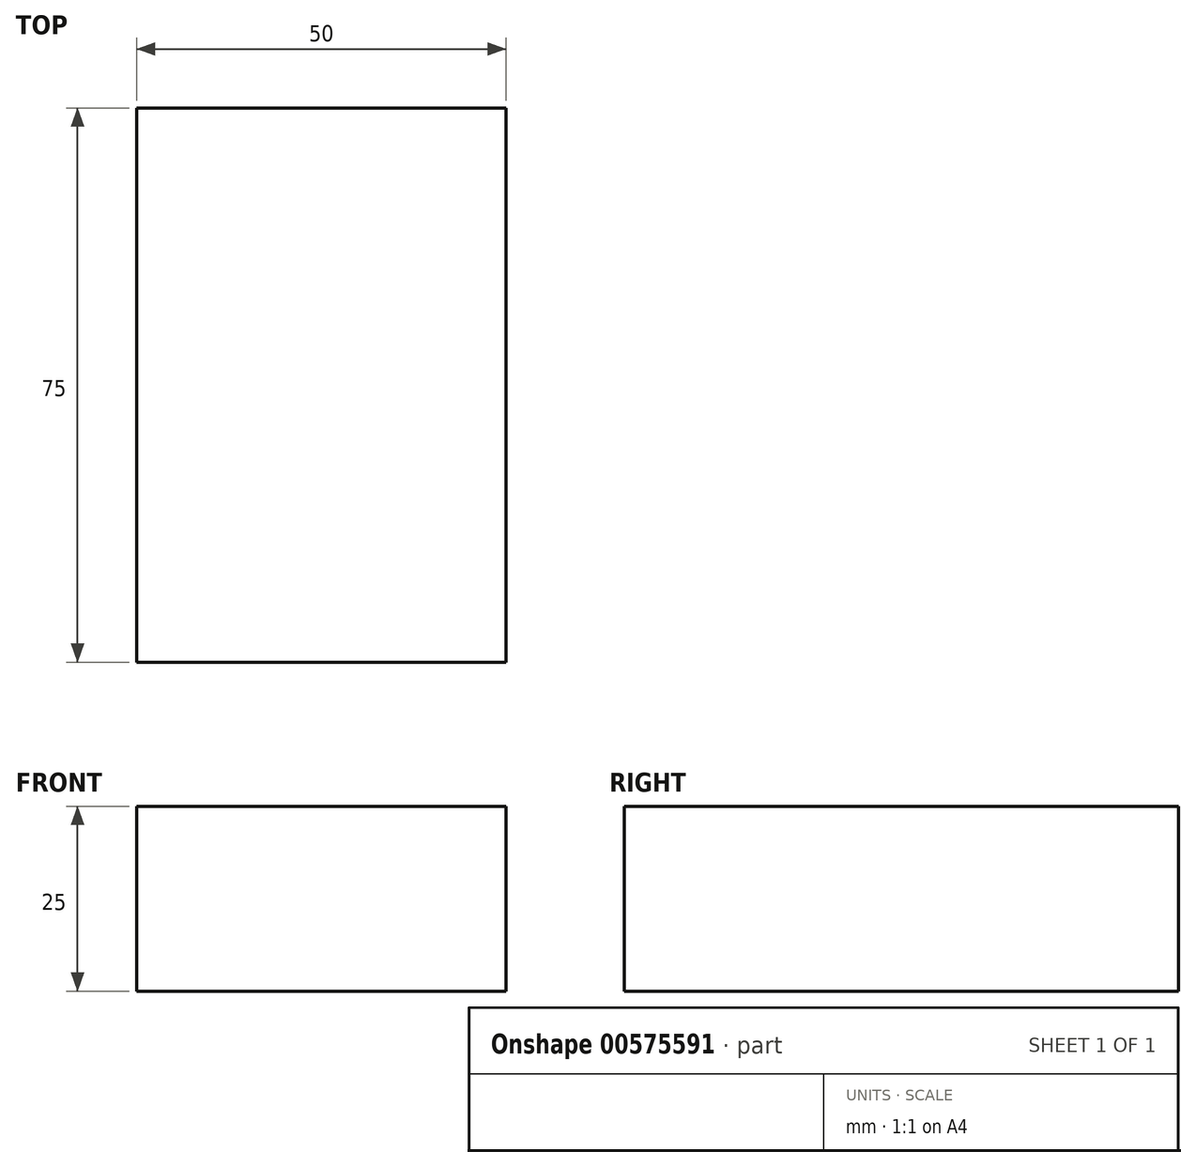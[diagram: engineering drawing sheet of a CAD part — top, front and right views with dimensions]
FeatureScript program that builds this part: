
annotation { "Feature Type Name" : "Feature", "Feature Type Description" : "" }
export const myFeature = defineFeature(function(context is Context, id is Id, definition is map)
    precondition{}
    {
        {
            var Q0;
            Q0=qCreatedBy(makeId("Top.planeOp"),FACE);
            var sketch = newSketch(context, id + "F0", { "sketchPlane" : qUnion([Q0])});
            skLineSegment(sketch, "E0.bottom", {"start": v(0, 0) * mm, "end": v(50, 0) * mm});
            skLineSegment(sketch, "E0.top", {"start": v(0, 75) * mm, "end": v(50, 75) * mm});
            skLineSegment(sketch, "E0.left", {"start": v(0, 0) * mm, "end": v(0, 75) * mm});
            skLineSegment(sketch, "E0.right", {"start": v(50, 0) * mm, "end": v(50, 75) * mm});
            skSolve(sketch);
        }
        {
            var Q0;
            Q0=makeQuery(id+"F0.imprint","IMPRINT",FACE,{"disambiguationData":[TD([[makeQuery(id+"F0.imprint","IMPRINT",EDGE,{"derivedFrom":sQuery(id+"F0.wireOp",EDGE,"E0.bottom")}),1.0]])]});
            extrude(context, id + "F1", {"entities" : qUnion([Q0]), "depth" : 25 * mm, "offsetDistance" : 25 * mm});
        }
    });
